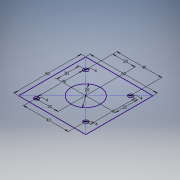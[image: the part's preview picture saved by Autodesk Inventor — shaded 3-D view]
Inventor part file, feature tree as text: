
AUTODESK INVENTOR PART (.ipt)
format: ipt  version: 2019 (Build 230136000, 136)  size: 101,376 bytes
history: native  units: mm
features: sketch x1
ambient origin geometry x8: Origin, YZ Plane, XZ Plane, XY Plane, X Axis, Y Axis, Z Axis, Center Point
feature tree (1):
  sketch  "Boceto1"  dims[d0=26.0mm d1=60.0mm d2=60.0mm d3=4.0mm d4=4.0mm d5=4.0mm d6=4.0mm d7=40.0mm d8=20.0mm d9=20.0mm d10=40.0mm d11=40.0mm d12=20.0mm d13=40.0mm d14=20.0mm]
